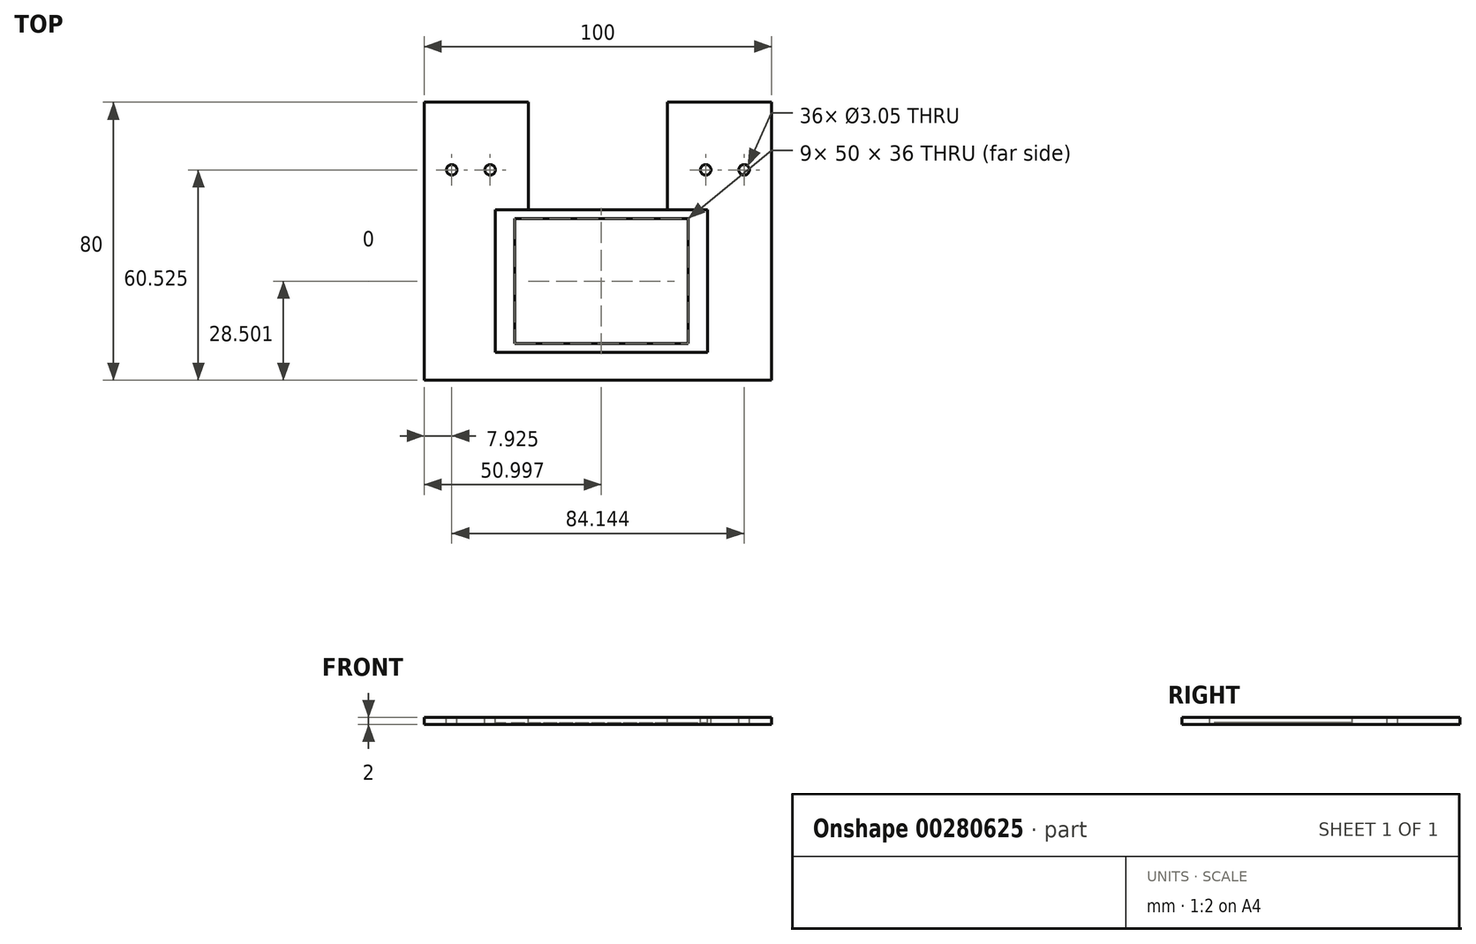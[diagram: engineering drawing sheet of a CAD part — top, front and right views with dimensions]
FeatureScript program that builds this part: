
annotation { "Feature Type Name" : "Feature", "Feature Type Description" : "" }
export const myFeature = defineFeature(function(context is Context, id is Id, definition is map)
    precondition{}
    {
        {
            var Q0;
            Q0=qCreatedBy(makeId("Top.planeOp"),FACE);
            var sketch = newSketch(context, id + "F0", { "sketchPlane" : qUnion([Q0])});
            skLineSegment(sketch, "E0.bottom", {"start": v(-41.91, 29.58) * mm, "end": v(58.09, 29.58) * mm});
            skLineSegment(sketch, "E0.top", {"start": v(-41.91, -50.42) * mm, "end": v(58.09, -50.42) * mm});
            skLineSegment(sketch, "E0.left", {"start": v(-41.91, 29.58) * mm, "end": v(-41.91, -50.42) * mm});
            skLineSegment(sketch, "E0.right", {"start": v(58.09, 29.58) * mm, "end": v(58.09, -50.42) * mm});
            skSolve(sketch);
        }
        {
            var Q0;
            Q0 = qSketchRegion(id + "F0", true);
            extrude(context, id + "F1", {"entities" : qUnion([Q0]), "depth" : 2 * mm});
        }
        {
            var Q0;
            Q0=makeQuery(id+"F1.opExtrude","CAP_FACE",FACE,{"disambiguationData":[OSD([sQuery(id+"F0.wireOp",EDGE,"E0.bottom"),sQuery(id+"F0.wireOp",EDGE,"E0.top"),sQuery(id+"F0.wireOp",EDGE,"E0.left"),sQuery(id+"F0.wireOp",EDGE,"E0.right")])],"isStart":false});
            var sketch = newSketch(context, id + "F2", { "sketchPlane" : qUnion([Q0])});
            skLineSegment(sketch, "E1.bottom", {"start": v(-11.91, 29.58) * mm, "end": v(28.09, 29.58) * mm});
            skLineSegment(sketch, "E1.top", {"start": v(-11.91, -1.42) * mm, "end": v(28.09, -1.42) * mm});
            skLineSegment(sketch, "E1.left", {"start": v(-11.91, 29.58) * mm, "end": v(-11.91, -1.42) * mm});
            skLineSegment(sketch, "E1.right", {"start": v(28.09, 29.58) * mm, "end": v(28.09, -1.42) * mm});
            skSolve(sketch);
        }
        {
            var Q0;
            Q0 = qSketchRegion(id + "F2", true);
            extrude(context, id + "F3", {"entities" : qUnion([Q0]), "operationType" : NewBodyOperationType.REMOVE, "endBound" : BoundingType.THROUGH_ALL, "oppositeDirection" : true, "depth" : 25.4 * mm});
        }
        {
            var Q0;
            Q0=makeQuery(id+"F1.opExtrude","CAP_FACE",FACE,{"disambiguationData":[OSD([sQuery(id+"F0.wireOp",EDGE,"E0.bottom"),sQuery(id+"F0.wireOp",EDGE,"E0.top"),sQuery(id+"F0.wireOp",EDGE,"E0.left"),sQuery(id+"F0.wireOp",EDGE,"E0.right")])],"isStart":false});
            var sketch = newSketch(context, id + "F4", { "sketchPlane" : qUnion([Q0])});
            skLineSegment(sketch, "E2.bottom", {"start": v(-21.41, -1.42) * mm, "end": v(39.59, -1.42) * mm});
            skLineSegment(sketch, "E2.top", {"start": v(-21.41, -42.42) * mm, "end": v(39.59, -42.42) * mm});
            skLineSegment(sketch, "E2.left", {"start": v(-21.41, -1.42) * mm, "end": v(-21.41, -42.42) * mm});
            skLineSegment(sketch, "E2.right", {"start": v(39.59, -1.42) * mm, "end": v(39.59, -42.42) * mm});
            skSolve(sketch);
        }
        {
            var Q0;
            Q0 = qSketchRegion(id + "F4", true);
            extrude(context, id + "F5", {"entities" : qUnion([Q0]), "operationType" : NewBodyOperationType.REMOVE, "oppositeDirection" : true, "depth" : 1.5 * mm});
        }
        {
            var Q0;
            Q0=makeQuery(id+"F1.opExtrude","CAP_FACE",FACE,{"disambiguationData":[OSD([sQuery(id+"F0.wireOp",EDGE,"E0.bottom"),sQuery(id+"F0.wireOp",EDGE,"E0.top"),sQuery(id+"F0.wireOp",EDGE,"E0.left"),sQuery(id+"F0.wireOp",EDGE,"E0.right")])],"isStart":false});
            var sketch = newSketch(context, id + "F6", { "sketchPlane" : qUnion([Q0])});
            skCircle(sketch, "E3", {"center": v(-33.99, 10.1) * mm, "radius": 1.52 * mm});
            skCircle(sketch, "E4", {"center": v(-22.94, 10.1) * mm, "radius": 1.52 * mm});
            skCircle(sketch, "E5", {"center": v(50.16, 10.1) * mm, "radius": 1.52 * mm});
            skCircle(sketch, "E6", {"center": v(39.11, 10.1) * mm, "radius": 1.52 * mm});
            skSolve(sketch);
        }
        {
            var Q0;
            Q0 = qSketchRegion(id + "F6", true);
            extrude(context, id + "F7", {"entities" : qUnion([Q0]), "operationType" : NewBodyOperationType.REMOVE, "endBound" : BoundingType.THROUGH_ALL, "oppositeDirection" : true, "depth" : 25.4 * mm});
        }
        {
            var Q0;
            Q0=makeQuery(id+"F5.boolean.opBoolean","COPY",FACE,{"derivedFrom":makeQuery(id+"F5.opExtrude","CAP_FACE",FACE,{"disambiguationData":[OSD([sQuery(id+"F4.wireOp",EDGE,"E2.bottom"),sQuery(id+"F4.wireOp",EDGE,"E2.top"),sQuery(id+"F4.wireOp",EDGE,"E2.left"),sQuery(id+"F4.wireOp",EDGE,"E2.right")])],"isStart":false})});
            var sketch = newSketch(context, id + "F8", { "sketchPlane" : qUnion([Q0])});
            skLineSegment(sketch, "E7.bottom", {"start": v(-15.91, -3.92) * mm, "end": v(34.09, -3.92) * mm});
            skLineSegment(sketch, "E7.top", {"start": v(-15.91, -39.92) * mm, "end": v(34.09, -39.92) * mm});
            skLineSegment(sketch, "E7.left", {"start": v(-15.91, -3.92) * mm, "end": v(-15.91, -39.92) * mm});
            skLineSegment(sketch, "E7.right", {"start": v(34.09, -3.92) * mm, "end": v(34.09, -39.92) * mm});
            skSolve(sketch);
        }
        {
            var Q0;
            Q0 = qSketchRegion(id + "F8", true);
            extrude(context, id + "F9", {"entities" : qUnion([Q0]), "operationType" : NewBodyOperationType.REMOVE, "endBound" : BoundingType.THROUGH_ALL, "oppositeDirection" : true, "depth" : 25.4 * mm});
        }
    });
